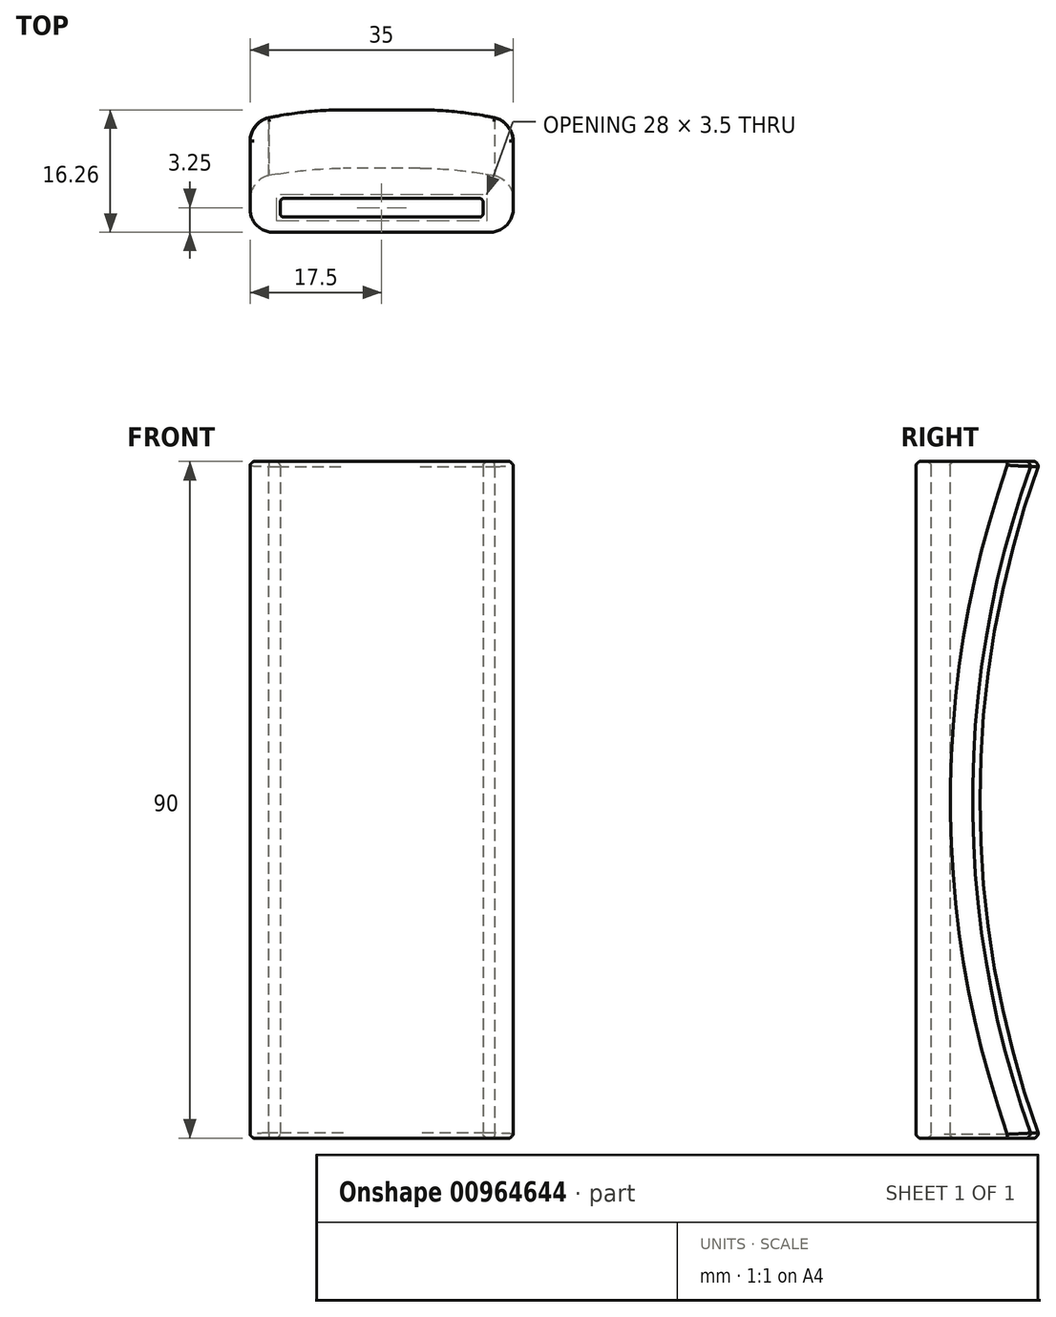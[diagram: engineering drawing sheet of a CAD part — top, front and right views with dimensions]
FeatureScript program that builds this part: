
annotation { "Feature Type Name" : "Feature", "Feature Type Description" : "" }
export const myFeature = defineFeature(function(context is Context, id is Id, definition is map)
    precondition{}
    {
        {
            var Q0;
            Q0=qCreatedBy(makeId("Top.planeOp"),FACE);
            var sketch = newSketch(context, id + "F0", { "sketchPlane" : qUnion([Q0])});
            skLineSegment(sketch, "E0.rect.bottom", {"start": v(13.5, 1.25) * mm, "end": v(-13.5, 1.25) * mm});
            skLineSegment(sketch, "E0.rect.top", {"start": v(13.5, -1.25) * mm, "end": v(-13.5, -1.25) * mm});
            skLineSegment(sketch, "E0.rect.left", {"start": v(13.5, 1.25) * mm, "end": v(13.5, -1.25) * mm});
            skLineSegment(sketch, "E0.rect.right", {"start": v(-13.5, 1.25) * mm, "end": v(-13.5, -1.25) * mm});
            skPoint(sketch, "E0.rect.middle", {"position": v(0, 0) * mm});
            skLineSegment(sketch, "E1.bottom", {"start": v(-17.5, 13.25) * mm, "end": v(17.5, 13.25) * mm});
            skLineSegment(sketch, "E1.top", {"start": v(-17.5, -3.25) * mm, "end": v(17.5, -3.25) * mm});
            skLineSegment(sketch, "E1.left", {"start": v(-17.5, 13.25) * mm, "end": v(-17.5, -3.25) * mm});
            skLineSegment(sketch, "E1.right", {"start": v(17.5, 13.25) * mm, "end": v(17.5, -3.25) * mm});
            skSolve(sketch);
        }
        {
            var Q0;
            Q0=makeQuery(id+"F0.imprint","IMPRINT",FACE,{"disambiguationData":[TD([[makeQuery(id+"F0.imprint","IMPRINT",EDGE,{"derivedFrom":sQuery(id+"F0.wireOp",EDGE,"E0.rect.bottom")}),-1.0]])]});
            extrude(context, id + "F1", {"entities" : qUnion([Q0]), "endBound" : BoundingType.SYMMETRIC, "depth" : 90 * mm});
        }
        {
            var Q0;
            Q0=qCreatedBy(makeId("Right.planeOp"),FACE);
            var sketch = newSketch(context, id + "F2", { "sketchPlane" : qUnion([Q0])});
            skLineSegment(sketch, "E2", {"start": v(13.25, -45) * mm, "end": v(13.25, 45) * mm});
            skArc(sketch, "E3", {"start": v(13.25, 45) * mm, "mid": v(5.25, 0) * mm, "end": v(13.25, -45) * mm});
            skLineSegment(sketch, "E4", {"start": v(13.25, 0) * mm, "end": v(5.25, 0) * mm});
            skSolve(sketch);
        }
        {
            var Q0;
            Q0=qSketchRegion(id+"F2",true);
            extrude(context, id + "F3", {"entities" : qUnion([Q0]), "operationType" : NewBodyOperationType.REMOVE, "endBound" : BoundingType.THROUGH_ALL, "depth" : 25 * mm, "hasSecondDirection" : true, "secondDirectionBound" : SecondDirectionBoundingType.THROUGH_ALL, "secondDirectionOppositeDirection" : true, "secondDirectionDepth" : 25 * mm});
        }
        {
            var Q0;
            Q0=makeQuery(id+"F3.boolean.opBoolean","INTERSECT",EDGE,{"derivedFrom":[makeQuery(id+"F1.opExtrude","SWEPT_FACE",FACE,{"disambiguationData":[OSD([sQuery(id+"F0.wireOp",EDGE,"E1.right")])]}),makeQuery(id+"F3.opExtrude","SWEPT_FACE",FACE,{"disambiguationData":[OSD([sQuery(id+"F2.wireOp",EDGE,"E3")])]})]});
            var Q1;
            Q1=makeQuery(id+"F3.boolean.opBoolean","INTERSECT",EDGE,{"derivedFrom":[makeQuery(id+"F1.opExtrude","SWEPT_FACE",FACE,{"disambiguationData":[OSD([sQuery(id+"F0.wireOp",EDGE,"E1.left")])]}),makeQuery(id+"F3.opExtrude","SWEPT_FACE",FACE,{"disambiguationData":[OSD([sQuery(id+"F2.wireOp",EDGE,"E3")])]})]});
            chamfer(context, id + "F4", {"entities" : qUnion([Q0, Q1]), "chamferType" : ChamferType.OFFSET_ANGLE, "width" : 8 * mm, "oppositeDirection" : true, "angle" : 10 * degree, "tangentPropagation" : true});
        }
        {
            var Q0;
            Q0=makeQuery(id+"F1.opExtrude","SWEPT_EDGE",EDGE,{"disambiguationData":[OSD([sQuery(id+"F0.wireOp",EDGE,"E1.top"),sQuery(id+"F0.wireOp",EDGE,"E1.left")])]});
            var Q1;
            Q1=makeQuery(id+"F1.opExtrude","SWEPT_EDGE",EDGE,{"disambiguationData":[OSD([sQuery(id+"F0.wireOp",EDGE,"E1.top"),sQuery(id+"F0.wireOp",EDGE,"E1.right")])]});
            var Q2;
            {var subQ0=makeQuery(id+"F1.opExtrude","SWEPT_FACE",FACE,{"disambiguationData":[OSD([sQuery(id+"F0.wireOp",EDGE,"E1.right")])]});Q2=makeQuery(id+"F4.opChamfer","BLEND_EDGE",EDGE,{"blendedFrom":[makeQuery(id+"F3.boolean.opBoolean","INTERSECT",EDGE,{"derivedFrom":[subQ0,makeQuery(id+"F3.opExtrude","SWEPT_FACE",FACE,{"disambiguationData":[OSD([sQuery(id+"F2.wireOp",EDGE,"E3")])]})]}),subQ0],"blendedInto":[subQ0]});}
            var Q3;
            {var subQ0=makeQuery(id+"F1.opExtrude","SWEPT_FACE",FACE,{"disambiguationData":[OSD([sQuery(id+"F0.wireOp",EDGE,"E1.left")])]});Q3=makeQuery(id+"F4.opChamfer","BLEND_EDGE",EDGE,{"blendedFrom":[makeQuery(id+"F3.boolean.opBoolean","INTERSECT",EDGE,{"derivedFrom":[subQ0,makeQuery(id+"F3.opExtrude","SWEPT_FACE",FACE,{"disambiguationData":[OSD([sQuery(id+"F2.wireOp",EDGE,"E3")])]})]}),subQ0],"blendedInto":[subQ0]});}
            fillet(context, id + "F5", {"entities" : qUnion([Q0, Q1, Q2, Q3]), "radius" : 3 * mm, "tangentPropagation" : true, "rho" : .4, "crossSection" : FilletCrossSection.CONIC, "allowEdgeOverflow" : false});
        }
        {
            var Q0;
            {var subQ0=makeQuery(id+"F3.opExtrude","SWEPT_FACE",FACE,{"disambiguationData":[OSD([sQuery(id+"F2.wireOp",EDGE,"E3")])]});Q0=makeQuery(id+"F4.opChamfer","BLEND_EDGE",EDGE,{"blendedFrom":[makeQuery(id+"F3.boolean.opBoolean","INTERSECT",EDGE,{"derivedFrom":[makeQuery(id+"F1.opExtrude","SWEPT_FACE",FACE,{"disambiguationData":[OSD([sQuery(id+"F0.wireOp",EDGE,"E1.right")])]}),subQ0]}),makeQuery(id+"F3.boolean.opBoolean","COPY",FACE,{"derivedFrom":subQ0})],"blendedInto":[makeQuery(id+"F3.boolean.opBoolean","COPY",FACE,{"derivedFrom":subQ0})]});}
            var Q1;
            {var subQ0=makeQuery(id+"F3.opExtrude","SWEPT_FACE",FACE,{"disambiguationData":[OSD([sQuery(id+"F2.wireOp",EDGE,"E3")])]});Q1=makeQuery(id+"F4.opChamfer","BLEND_EDGE",EDGE,{"blendedFrom":[makeQuery(id+"F3.boolean.opBoolean","INTERSECT",EDGE,{"derivedFrom":[makeQuery(id+"F1.opExtrude","SWEPT_FACE",FACE,{"disambiguationData":[OSD([sQuery(id+"F0.wireOp",EDGE,"E1.left")])]}),subQ0]}),makeQuery(id+"F3.boolean.opBoolean","COPY",FACE,{"derivedFrom":subQ0})],"blendedInto":[makeQuery(id+"F3.boolean.opBoolean","COPY",FACE,{"derivedFrom":subQ0})]});}
            fillet(context, id + "F6", {"entities" : qUnion([Q0, Q1]), "radius" : 50 * mm, "tangentPropagation" : true, "allowEdgeOverflow" : false});
        }
        {
            var Q0;
            Q0=makeQuery(id+"F1.opExtrude","SWEPT_EDGE",EDGE,{"disambiguationData":[OSD([sQuery(id+"F0.wireOp",EDGE,"E0.rect.top"),sQuery(id+"F0.wireOp",EDGE,"E0.rect.left")])]});
            var Q1;
            Q1=makeQuery(id+"F1.opExtrude","SWEPT_EDGE",EDGE,{"disambiguationData":[OSD([sQuery(id+"F0.wireOp",EDGE,"E0.rect.bottom"),sQuery(id+"F0.wireOp",EDGE,"E0.rect.left")])]});
            var Q2;
            Q2=makeQuery(id+"F1.opExtrude","SWEPT_EDGE",EDGE,{"disambiguationData":[OSD([sQuery(id+"F0.wireOp",EDGE,"E0.rect.top"),sQuery(id+"F0.wireOp",EDGE,"E0.rect.right")])]});
            var Q3;
            Q3=makeQuery(id+"F1.opExtrude","SWEPT_EDGE",EDGE,{"disambiguationData":[OSD([sQuery(id+"F0.wireOp",EDGE,"E0.rect.bottom"),sQuery(id+"F0.wireOp",EDGE,"E0.rect.right")])]});
            fillet(context, id + "F7", {"entities" : qUnion([Q0, Q1, Q2, Q3]), "radius" : .5 * mm, "tangentPropagation" : true, "allowEdgeOverflow" : false});
        }
        {
            var Q0;
            Q0=makeQuery(id+"F1.opExtrude","CAP_FACE",FACE,{"disambiguationData":[OSD([sQuery(id+"F0.wireOp",EDGE,"E0.rect.bottom"),sQuery(id+"F0.wireOp",EDGE,"E0.rect.top"),sQuery(id+"F0.wireOp",EDGE,"E0.rect.left"),sQuery(id+"F0.wireOp",EDGE,"E0.rect.right"),sQuery(id+"F0.wireOp",EDGE,"E1.bottom"),sQuery(id+"F0.wireOp",EDGE,"E1.top"),sQuery(id+"F0.wireOp",EDGE,"E1.left"),sQuery(id+"F0.wireOp",EDGE,"E1.right")])],"isStart":true});
            var Q1;
            Q1=makeQuery(id+"F1.opExtrude","CAP_FACE",FACE,{"disambiguationData":[OSD([sQuery(id+"F0.wireOp",EDGE,"E0.rect.bottom"),sQuery(id+"F0.wireOp",EDGE,"E0.rect.top"),sQuery(id+"F0.wireOp",EDGE,"E0.rect.left"),sQuery(id+"F0.wireOp",EDGE,"E0.rect.right"),sQuery(id+"F0.wireOp",EDGE,"E1.bottom"),sQuery(id+"F0.wireOp",EDGE,"E1.top"),sQuery(id+"F0.wireOp",EDGE,"E1.left"),sQuery(id+"F0.wireOp",EDGE,"E1.right")])],"isStart":false});
            fillet(context, id + "F8", {"entities" : qUnion([Q0, Q1]), "radius" : .5 * mm, "tangentPropagation" : true, "rho" : .2, "crossSection" : FilletCrossSection.CONIC, "allowEdgeOverflow" : false});
        }
    });
